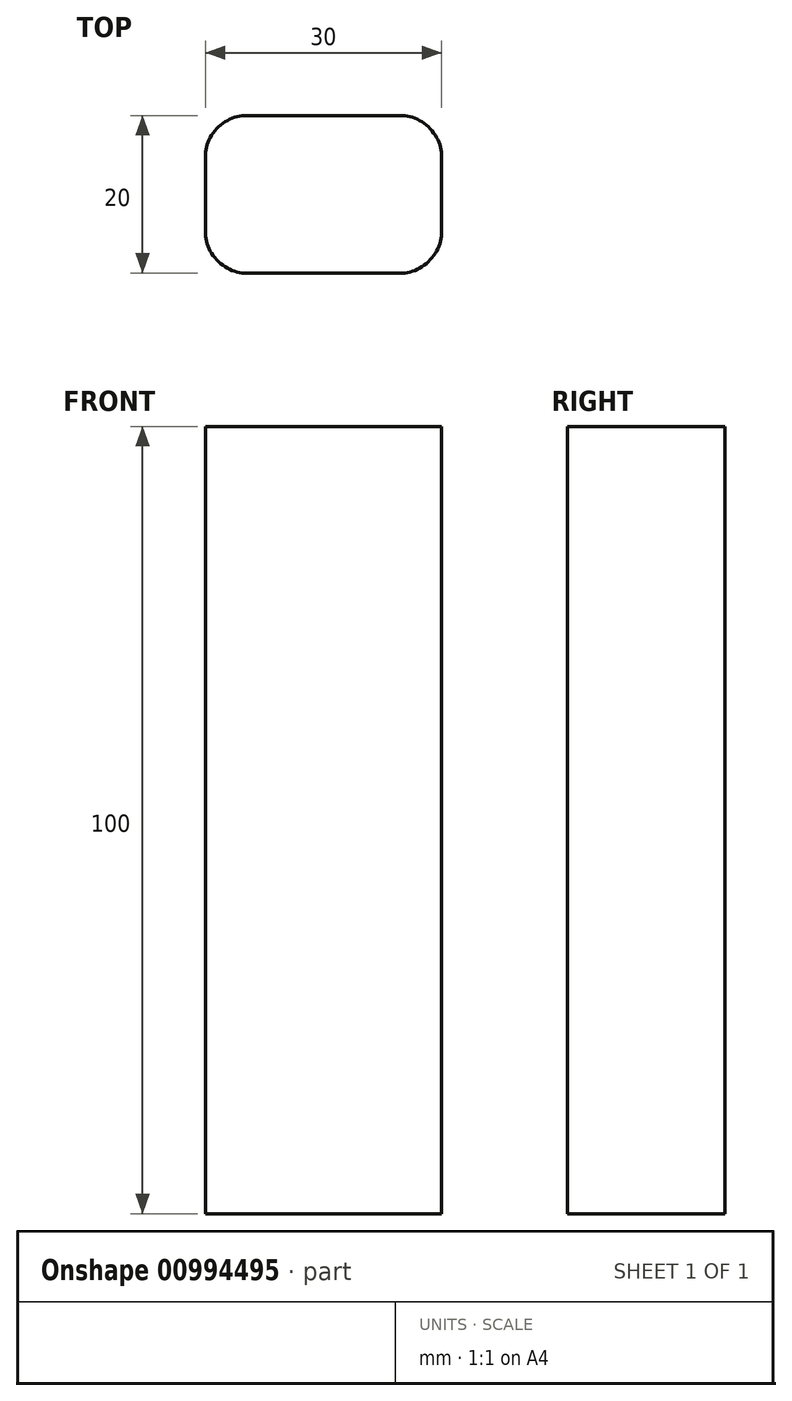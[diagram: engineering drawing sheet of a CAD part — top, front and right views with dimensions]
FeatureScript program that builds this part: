
annotation { "Feature Type Name" : "Feature", "Feature Type Description" : "" }
export const myFeature = defineFeature(function(context is Context, id is Id, definition is map)
    precondition{}
    {
        {
            var Q0;
            Q0=qCreatedBy(makeId("Top.planeOp"),FACE);
            var sketch = newSketch(context, id + "F0", { "sketchPlane" : qUnion([Q0])});
            skLineSegment(sketch, "E0.bottom", {"start": v(15, 10) * mm, "end": v(10, 10) * mm});
            skLineSegment(sketch, "E0.top", {"start": v(15, -10) * mm, "end": v(10, -10) * mm});
            skLineSegment(sketch, "E0.left", {"start": v(15, 10) * mm, "end": v(15, 5) * mm});
            skLineSegment(sketch, "E0.right", {"start": v(-15, 10) * mm, "end": v(-15, 5) * mm});
            skPoint(sketch, "E0.middle", {"position": v(0, 0) * mm});
            skLineSegment(sketch, "E1", {"start": v(-15, 5) * mm, "end": v(-15, -5) * mm});
            skLineSegment(sketch, "E2", {"start": v(-10, 10) * mm, "end": v(-15, 10) * mm});
            skLineSegment(sketch, "E3", {"start": v(10, 10) * mm, "end": v(-10, 10) * mm});
            skLineSegment(sketch, "E4", {"start": v(15, 5) * mm, "end": v(15, -5) * mm});
            skLineSegment(sketch, "E5", {"start": v(15, -5) * mm, "end": v(15, -10) * mm});
            skLineSegment(sketch, "E6", {"start": v(10, -10) * mm, "end": v(-10, -10) * mm});
            skLineSegment(sketch, "E7", {"start": v(-10, -10) * mm, "end": v(-15, -10) * mm});
            skLineSegment(sketch, "E8", {"start": v(-15, -5) * mm, "end": v(-15, -10) * mm});
            skPoint(sketch, "E9", {"position": v(0, 10) * mm});
            skPoint(sketch, "E10", {"position": v(0, -10) * mm});
            skPoint(sketch, "E11", {"position": v(-15, 0) * mm});
            skPoint(sketch, "E12", {"position": v(15, 0) * mm});
            skFitSpline(sketch, "E13", {"points": [v(-10, 10) * mm, v(-15, 5) * mm], "startDerivative": vector(-7.5, 0) * mm, "endDerivative": vector(0, -7.5) * mm});
            skFitSpline(sketch, "E14", {"points": [v(10, 10) * mm, v(15, 5) * mm], "startDerivative": vector(7.5, 0) * mm, "endDerivative": vector(0, -7.5) * mm});
            skFitSpline(sketch, "E15", {"points": [v(15, -5) * mm, v(10, -10) * mm], "startDerivative": vector(0, -7.5) * mm, "endDerivative": vector(-7.5, 0) * mm});
            skFitSpline(sketch, "E16", {"points": [v(-10, -10) * mm, v(-15, -5) * mm], "startDerivative": vector(-7.5, 0) * mm, "endDerivative": vector(0, 7.5) * mm});
            skSolve(sketch);
        }
        {
            var Q0;
            Q0=makeQuery(id+"F0.imprint","IMPRINT",FACE,{"disambiguationData":[TD([[makeQuery(id+"F0.imprint","IMPRINT",EDGE,{"derivedFrom":sQuery(id+"F0.wireOp",EDGE,"E1")}),1.0]])]});
            extrude(context, id + "F1", {"entities" : qUnion([Q0]), "endBound" : BoundingType.SYMMETRIC, "depth" : 100 * mm, "offsetDistance" : 25 * mm});
        }
    });
